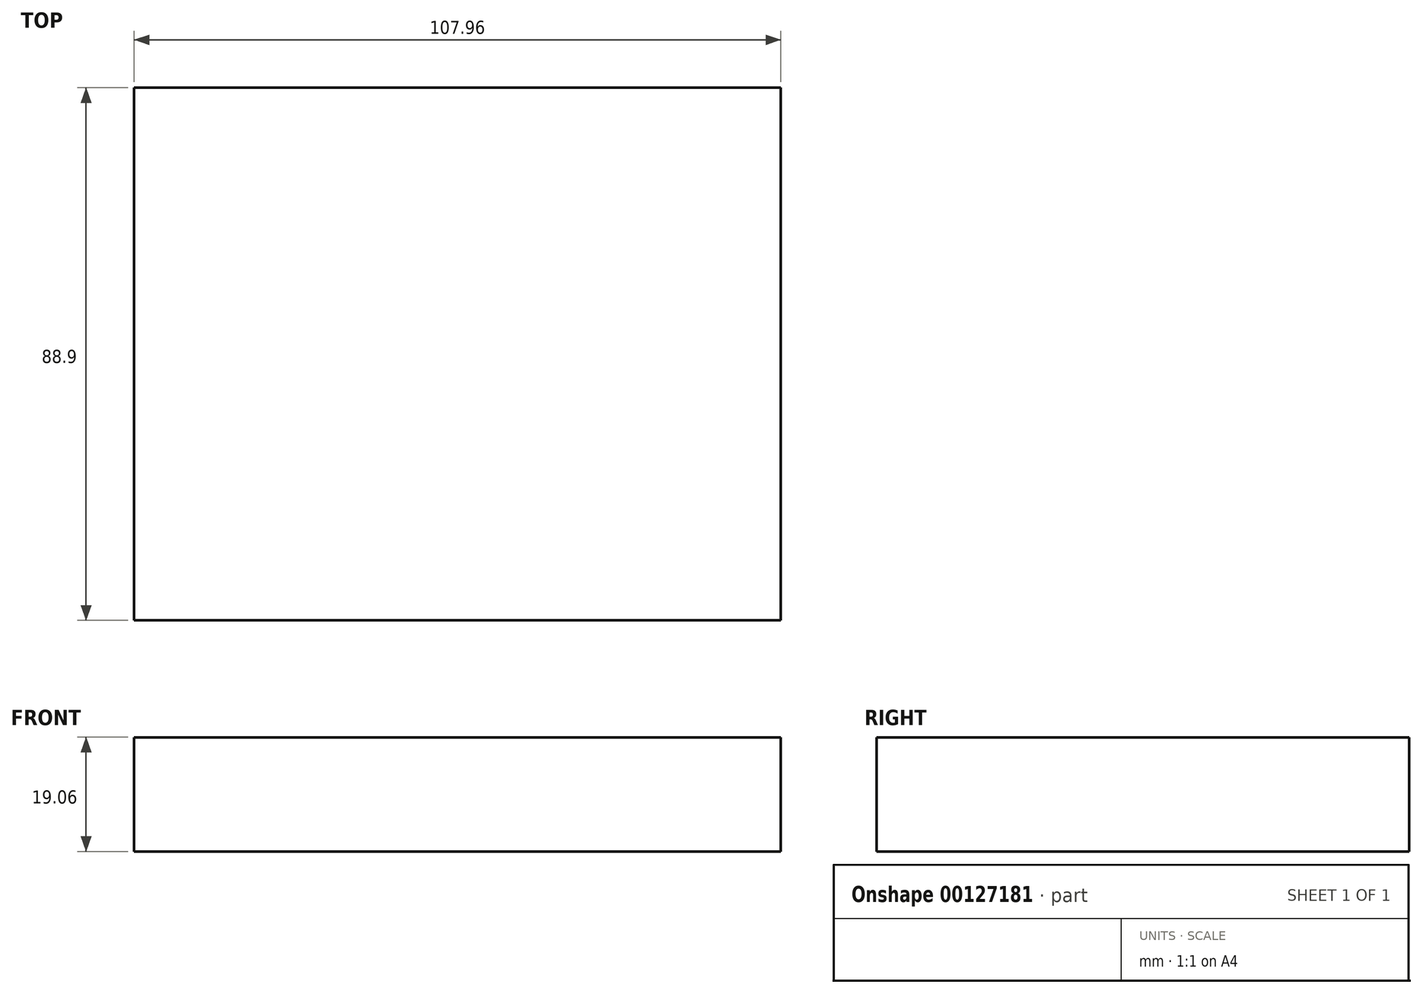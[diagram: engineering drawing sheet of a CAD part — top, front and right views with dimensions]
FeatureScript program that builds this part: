
annotation { "Feature Type Name" : "Feature", "Feature Type Description" : "" }
export const myFeature = defineFeature(function(context is Context, id is Id, definition is map)
    precondition{}
    {
        {
            var Q0;
            Q0=qCreatedBy(makeId("Front.planeOp"),FACE);
            var sketch = newSketch(context, id + "F0", { "sketchPlane" : qUnion([Q0])});
            skLineSegment(sketch, "E0.bottom", {"start": v(53.98, -9.52) * mm, "end": v(-53.98, -9.52) * mm});
            skLineSegment(sketch, "E0.top", {"start": v(53.98, 9.53) * mm, "end": v(-53.98, 9.52) * mm});
            skLineSegment(sketch, "E0.left", {"start": v(53.98, -9.52) * mm, "end": v(53.98, 9.53) * mm});
            skLineSegment(sketch, "E0.right", {"start": v(-53.98, -9.52) * mm, "end": v(-53.98, 9.53) * mm});
            skPoint(sketch, "E0.middle", {"position": v(0, 0) * mm});
            skSolve(sketch);
        }
        {
            var Q0;
            Q0=qSketchRegion(id+"F0",true);
            extrude(context, id + "F1", {"entities" : qUnion([Q0]), "depth" : 88.9 * mm});
        }
    });
